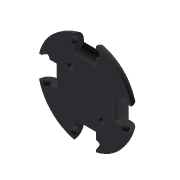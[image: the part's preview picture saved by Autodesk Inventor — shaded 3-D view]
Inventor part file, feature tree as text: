
AUTODESK INVENTOR PART (.ipt)
format: ipt  version: 2017 (Build 210142000, 142)  size: 168,448 bytes
history: native  units: mm
features: sketch x4, extrude x2, fillet x1, revolve x1, pattern_circular x1, hole x1
ambient origin geometry x8: Origin, YZ Plane, XZ Plane, XY Plane, X Axis, Y Axis, Z Axis, Center Point
bodies: Solid1 (feature_tree)
feature tree (10):
  extrude  "Extrusion1"  Depth=6.0mm TaperAngle=0.0deg
  fillet  "Fillet1"  Radius=6.0mm
  revolve  "Revolution1"  [1 undecoded]
  pattern_circular  "Circular Pattern1"  [2 undecoded]
  extrude  "Extrusion2"  TaperAngle=90.0deg  [1 undecoded]
  hole  "Hole1"  [1 undecoded]
  sketch  "Sketch1"  dims[d0=60.0mm d1=6.0mm d2=0.0mm d3=6.0mm]
  sketch  "Sketch2"  dims[d4=14.0mm d5=7.0mm]
  sketch  "Sketch3"  dims[d6=18.0mm]
  sketch  "Sketch4"  dims[d7=5.0mm d8=5.0mm d9=90.0deg d10=40.0mm d11=360.0deg d13=36.0mm d14=2.0mm d15=0.0mm d16=45.0deg d17=14.0mm d18=14.0mm d19=4.0mm d20=6.0mm d21=4.0mm d22=2.0mm d23=90.0deg d24=8.0mm d25=20.594885mm]
note: 5 required parameter values undecoded (feature->parameter linkage not recoverable at this tier; creation-order binding heuristic only, values carry confidence <= 0.55)